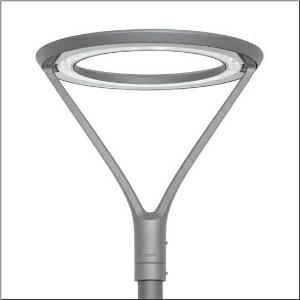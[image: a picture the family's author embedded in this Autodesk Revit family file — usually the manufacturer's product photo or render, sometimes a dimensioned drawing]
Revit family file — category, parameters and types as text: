
# Revit family: dl_r__20___pl1_2s_5xa512836s008_bfda
name_source: partatom
category: Lighting Fixtures
units: mm (PartAtom-declared; Revit-internal decimal feet)

## family parameters
Cut with Voids When Loaded = No
Host = Face
Light Source = No
Part Type = Normal
Room Calculation Point = No
Round Connector Dimension = Use Diameter
Shared = No

## types (1)
- --- (1 x LED, 3050 lm, 28.6 W, 2700K)
    Apparent Load = 29 VA
    CIE Flux Codes = 33 78 99 100 100
    Color Rendering = 70
    Color Temperature = 2700K
    Default Elevation = 1800 mm
    Description = DL® 20, mast luminaire, primary light control with reflector, highly specular, primary optical cover: cover, of toughened safety glass of clear glass with excellent transmission level, light distribution: PL1.2s, light emission: direct distribution, primary light characteristic: symmetric, installation type: post-top, LED, High Power LED, rated luminous flux: 3.050lm, luminous efficacy: 107lm/W, light colour: 727, colour temperature: 2700K, control gear: Plus, control: flexible luminous flux parameterisation, time-dependent luminous flux control, constant luminous flux control, digital communication interface, power reduction, overheat protection, electronic power reduction, mains connection: 220..240V, 50/60Hz, connection cable pre-assembled, cable length: 5m, start of lifetime: 29W, end of service life: 29W, reduction: 15W, luminaire housing, upper part, of cast aluminium, powder-coated, Siteco® metallic grey (DB 702S), diameter: 690mm, height: 690mm, spigot size: 76mm (post-top), mounting height: 4..6m, luminaire housing, of cast aluminium, powder-coated, Siteco® metallic grey (DB 702S), equipment: standard, protection rating (complete): IP66, insulation class (complete): insulation class II (safety insulation), certification: CE, ENEC, VDE, impact resistance: IK08, permissible operating ambient temperature: -25..+35°C, standard-compliant lighting for roads and squares, packaging unit: 1 piece

Light Distribution: PL1.2s
    Height = 690 mm
    Lamp = 1 x LED
    Lamp Light Flux = 3050 lm
    Lamp Power = 28.6 W
    Lamp count = 1
    Length = 690 mm
    Luminous efficacy = 107 lm/W
    Manufacturer = Siteco
    ModVariant = No
    Model = 5XA512836S008
    Number of Poles = 1
    OnlyDefault = Yes
    Power Factor = 1
    Product Name = DL® 20 | PL1.2s
    Product group = mast luminaire | pylon top
    ProductGroupID = 6100
    Protection Class = Protection class II
    Protection Degree = IP 66
    RLX_Detail_Level = 1
    RLX_Emergency_Light_Flux = 0 lm
    RLX_Emergency_Type = 0
    RLX_Emergency_Type_DB = No
    RlxData = <blob elided: 204289 chars, md5=74ff9a5a>
    Socket = socket
    Standby Power = 0 W
    System Light Flux = 3050 lm
    System Power = 29 W
    Type Comments = factory setting: luminous flux: 100 % | dim-lin: 254 | 386 mA
    Type Image = l_1006001.jpg
    URL = http://relux.com
    VarID = @adj_098345
    Voltage = 0 V
    Weight = 0.00 kg
    Width = 0 mm  [stored 0 ft]

note: [stored X ft] marks values corroborated as IEEE doubles in the binary element streams (Revit-internal decimal feet)

## geometry (parser evidence)
native form markers: Blend x4, Sweep x11
no freeform markers — native parametric forms only
